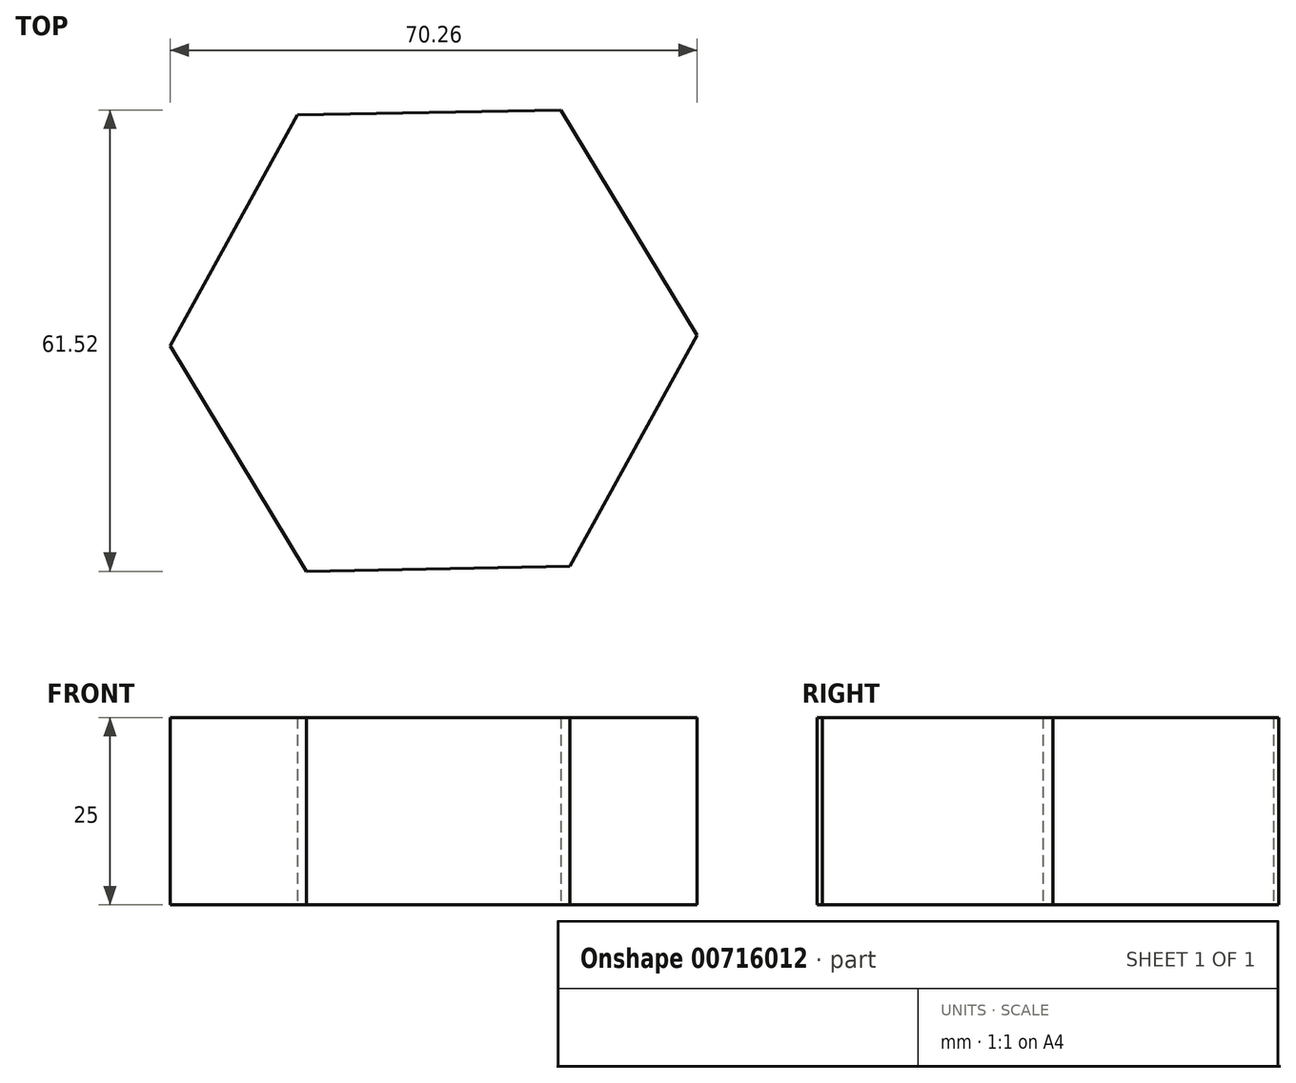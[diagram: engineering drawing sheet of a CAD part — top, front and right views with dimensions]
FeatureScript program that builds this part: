
annotation { "Feature Type Name" : "Feature", "Feature Type Description" : "" }
export const myFeature = defineFeature(function(context is Context, id is Id, definition is map)
    precondition{}
    {
        {
            var Q0;
            Q0=qCreatedBy(makeId("Top.planeOp"),FACE);
            var sketch = newSketch(context, id + "F0", { "sketchPlane" : qUnion([Q0])});
            skCircle(sketch, "E0.cCircle", {"center": v(0, 0) * mm, "radius": 30.43 * mm, "construction": true});
            skLineSegment(sketch, "E0.0", {"start": v(35.13, 0.68) * mm, "end": v(18.15, -30.08) * mm});
            skLineSegment(sketch, "E0.1", {"start": v(18.15, -30.08) * mm, "end": v(-16.98, -30.76) * mm});
            skLineSegment(sketch, "E0.2", {"start": v(-16.98, -30.76) * mm, "end": v(-35.13, -0.68) * mm});
            skLineSegment(sketch, "E0.3", {"start": v(-35.13, -0.68) * mm, "end": v(-18.15, 30.08) * mm});
            skLineSegment(sketch, "E0.4", {"start": v(-18.15, 30.08) * mm, "end": v(16.98, 30.76) * mm});
            skLineSegment(sketch, "E0.5", {"start": v(16.98, 30.76) * mm, "end": v(35.13, 0.68) * mm});
            skPoint(sketch, "E0.0.midPoint", {"position": v(26.64, -14.7) * mm});
            skSolve(sketch);
        }
        {
            var Q0;
            Q0=makeQuery(id+"F0.imprint","IMPRINT",FACE,{"disambiguationData":[TD([[makeQuery(id+"F0.imprint","IMPRINT",EDGE,{"derivedFrom":sQuery(id+"F0.wireOp",EDGE,"E0.0")}),-1.0]])]});
            extrude(context, id + "F1", {"entities" : qUnion([Q0]), "depth" : 25 * mm, "offsetDistance" : 25 * mm});
        }
    });
